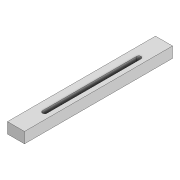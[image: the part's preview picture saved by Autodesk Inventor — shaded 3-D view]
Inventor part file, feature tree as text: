
AUTODESK INVENTOR PART (.ipt)
format: ipt  version: 2022 (Build 260153000, 153)  size: 90,624 bytes
history: native  units: mm
features: extrude x1, sketch x1
ambient origin geometry x8: Origin, YZ Plane, XZ Plane, XY Plane, X Axis, Y Axis, Z Axis, Center Point
bodies: Solid1 (feature_tree)
feature tree (2):
  extrude  "Extrusion1"  Depth=70.0mm
  sketch  "Sketch1"  dims[d0=3.3mm d1=70.0mm d2=10.0mm d3=10.0mm d4=20.0mm d5=20.0mm d6=6.0mm d7=8.0mm d8=0.0mm]
